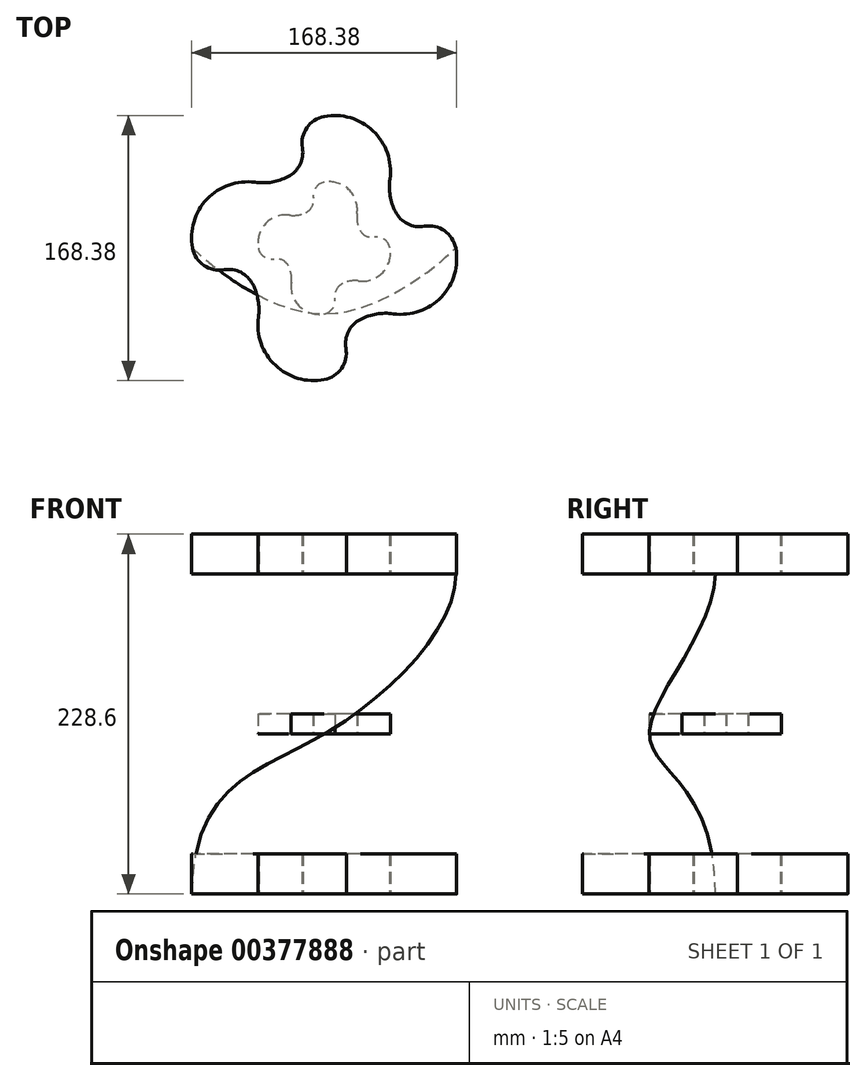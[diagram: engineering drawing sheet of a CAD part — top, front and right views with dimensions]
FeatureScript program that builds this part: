
annotation { "Feature Type Name" : "Feature", "Feature Type Description" : "" }
export const myFeature = defineFeature(function(context is Context, id is Id, definition is map)
    precondition{}
    {
        {
            var Q0;
            Q0=qCreatedBy(makeId("Top.planeOp"),FACE);
            var sketch = newSketch(context, id + "F0", { "sketchPlane" : qUnion([Q0])});
            skCircle(sketch, "E0", {"center": v(0, 0) * mm, "radius": 50.8 * mm, "construction": true});
            skArc(sketch, "E1", {"start": v(-23.02, 45.28) * mm, "mid": v(-15.4, 52.95) * mm, "end": v(-13.81, 63.64) * mm});
            skArc(sketch, "E2", {"start": v(0, 83.56) * mm, "mid": v(-10.98, 76.42) * mm, "end": v(-13.81, 63.64) * mm});
            skArc(sketch, "E3", {"start": v(41.76, 43.9) * mm, "mid": v(31.05, 74.44) * mm, "end": v(0, 83.56) * mm});
            skArc(sketch, "E4", {"start": v(41.76, 43.9) * mm, "mid": v(41.93, 33.2) * mm, "end": v(45.28, 23.02) * mm});
            skArc(sketch, "E5.1.0", {"start": v(-45.28, -23.02) * mm, "mid": v(-52.95, -15.4) * mm, "end": v(-63.64, -13.81) * mm});
            skArc(sketch, "E5.1.1", {"start": v(-83.56, 0) * mm, "mid": v(-76.42, -10.98) * mm, "end": v(-63.64, -13.81) * mm});
            skArc(sketch, "E5.1.2", {"start": v(-43.9, 41.76) * mm, "mid": v(-74.44, 31.05) * mm, "end": v(-83.56, 0) * mm});
            skArc(sketch, "E5.1.3", {"start": v(-43.9, 41.76) * mm, "mid": v(-33.2, 41.93) * mm, "end": v(-23.02, 45.28) * mm});
            skArc(sketch, "E5.2.0", {"start": v(23.02, -45.28) * mm, "mid": v(15.4, -52.95) * mm, "end": v(13.81, -63.64) * mm});
            skArc(sketch, "E5.2.1", {"start": v(0, -83.56) * mm, "mid": v(10.98, -76.42) * mm, "end": v(13.81, -63.64) * mm});
            skArc(sketch, "E5.2.2", {"start": v(-41.76, -43.9) * mm, "mid": v(-31.05, -74.44) * mm, "end": v(0, -83.56) * mm});
            skArc(sketch, "E5.2.3", {"start": v(-41.76, -43.9) * mm, "mid": v(-41.93, -33.2) * mm, "end": v(-45.28, -23.02) * mm});
            skArc(sketch, "E6.2.3.0", {"start": v(45.28, 23.02) * mm, "mid": v(52.95, 15.4) * mm, "end": v(63.64, 13.81) * mm});
            skArc(sketch, "E6.4.3.0", {"start": v(83.56, 0) * mm, "mid": v(76.42, 10.98) * mm, "end": v(63.64, 13.81) * mm});
            skArc(sketch, "E6.8.3.0", {"start": v(43.9, -41.76) * mm, "mid": v(74.44, -31.05) * mm, "end": v(83.56, 0) * mm});
            skArc(sketch, "E6.12.3.0", {"start": v(43.9, -41.76) * mm, "mid": v(33.2, -41.93) * mm, "end": v(23.02, -45.28) * mm});
            skSolve(sketch);
        }
        {
            var Q0;
            Q0=makeQuery(id+"F0.imprint","IMPRINT",FACE,{"disambiguationData":[TD([[makeQuery(id+"F0.imprint","IMPRINT",EDGE,{"derivedFrom":sQuery(id+"F0.wireOp",EDGE,"E1")}),-1.0]])]});
            extrude(context, id + "F1", {"entities" : qUnion([Q0]), "depth" : 25.4 * mm});
        }
        {
            var Q0;
            Q0=makeQuery(id+"F1.opExtrude","SWEPT_BODY",BODY,{"disambiguationData":[OSD([sQuery(id+"F0.wireOp",EDGE,"E1"),sQuery(id+"F0.wireOp",EDGE,"E2"),sQuery(id+"F0.wireOp",EDGE,"E3"),sQuery(id+"F0.wireOp",EDGE,"E4"),sQuery(id+"F0.wireOp",EDGE,"E5.1.0"),sQuery(id+"F0.wireOp",EDGE,"E5.1.1"),sQuery(id+"F0.wireOp",EDGE,"E5.1.2"),sQuery(id+"F0.wireOp",EDGE,"E5.1.3"),sQuery(id+"F0.wireOp",EDGE,"E5.2.0"),sQuery(id+"F0.wireOp",EDGE,"E5.2.1"),sQuery(id+"F0.wireOp",EDGE,"E5.2.2"),sQuery(id+"F0.wireOp",EDGE,"E5.2.3"),sQuery(id+"F0.wireOp",EDGE,"E6.2.3.0"),sQuery(id+"F0.wireOp",EDGE,"E6.4.3.0"),sQuery(id+"F0.wireOp",EDGE,"E6.8.3.0"),sQuery(id+"F0.wireOp",EDGE,"E6.12.3.0"),sQuery(id+"F0.wireOp",EDGE,"E6.2.4.0"),sQuery(id+"F0.wireOp",EDGE,"E6.4.4.0"),sQuery(id+"F0.wireOp",EDGE,"E6.8.4.0"),sQuery(id+"F0.wireOp",EDGE,"E6.12.4.0")])]});
            var Q1;
            Q1=qCreatedBy(makeId("Origin.pointOp"),VERTEX);
            transform(context, id + "F2", {"entities" : qUnion([Q0]), "transformType" : TransformType.TRANSLATION_3D, "dx" : 0 * mm, "dy" : 0 * mm, "dz" : 101.6 * mm, "makeCopy" : true});
        }
        {
            var Q0;
            Q0=makeQuery(id+"F2.opPattern","COPY",BODY,{"derivedFrom":makeQuery(id+"F1.opExtrude","SWEPT_BODY",BODY,{"disambiguationData":[OSD([sQuery(id+"F0.wireOp",EDGE,"E1"),sQuery(id+"F0.wireOp",EDGE,"E2"),sQuery(id+"F0.wireOp",EDGE,"E3"),sQuery(id+"F0.wireOp",EDGE,"E4"),sQuery(id+"F0.wireOp",EDGE,"E5.1.0"),sQuery(id+"F0.wireOp",EDGE,"E5.1.1"),sQuery(id+"F0.wireOp",EDGE,"E5.1.2"),sQuery(id+"F0.wireOp",EDGE,"E5.1.3"),sQuery(id+"F0.wireOp",EDGE,"E5.2.0"),sQuery(id+"F0.wireOp",EDGE,"E5.2.1"),sQuery(id+"F0.wireOp",EDGE,"E5.2.2"),sQuery(id+"F0.wireOp",EDGE,"E5.2.3"),sQuery(id+"F0.wireOp",EDGE,"E6.2.3.0"),sQuery(id+"F0.wireOp",EDGE,"E6.4.3.0"),sQuery(id+"F0.wireOp",EDGE,"E6.8.3.0"),sQuery(id+"F0.wireOp",EDGE,"E6.12.3.0"),sQuery(id+"F0.wireOp",EDGE,"E6.2.4.0"),sQuery(id+"F0.wireOp",EDGE,"E6.4.4.0"),sQuery(id+"F0.wireOp",EDGE,"E6.8.4.0"),sQuery(id+"F0.wireOp",EDGE,"E6.12.4.0")])]}),"instanceName":"1"});
            transform(context, id + "F3", {"entities" : qUnion([Q0]), "transformType" : TransformType.TRANSLATION_3D, "dx" : 0 * mm, "dy" : 0 * mm, "dz" : 101.6 * mm, "makeCopy" : true});
        }
        {
            var Q0;
            Q0=makeQuery(id+"F2.opPattern","COPY",FACE,{"derivedFrom":makeQuery(id+"F1.opExtrude","CAP_FACE",FACE,{"disambiguationData":[OSD([sQuery(id+"F0.wireOp",EDGE,"E1"),sQuery(id+"F0.wireOp",EDGE,"E2"),sQuery(id+"F0.wireOp",EDGE,"E3"),sQuery(id+"F0.wireOp",EDGE,"E4"),sQuery(id+"F0.wireOp",EDGE,"E5.1.0"),sQuery(id+"F0.wireOp",EDGE,"E5.1.1"),sQuery(id+"F0.wireOp",EDGE,"E5.1.2"),sQuery(id+"F0.wireOp",EDGE,"E5.1.3"),sQuery(id+"F0.wireOp",EDGE,"E5.2.0"),sQuery(id+"F0.wireOp",EDGE,"E5.2.1"),sQuery(id+"F0.wireOp",EDGE,"E5.2.2"),sQuery(id+"F0.wireOp",EDGE,"E5.2.3"),sQuery(id+"F0.wireOp",EDGE,"E6.2.3.0"),sQuery(id+"F0.wireOp",EDGE,"E6.4.3.0"),sQuery(id+"F0.wireOp",EDGE,"E6.8.3.0"),sQuery(id+"F0.wireOp",EDGE,"E6.12.3.0"),sQuery(id+"F0.wireOp",EDGE,"E6.2.4.0"),sQuery(id+"F0.wireOp",EDGE,"E6.4.4.0"),sQuery(id+"F0.wireOp",EDGE,"E6.8.4.0"),sQuery(id+"F0.wireOp",EDGE,"E6.12.4.0")])],"isStart":true}),"instanceName":"1"});
            var sketch = newSketch(context, id + "F4", { "sketchPlane" : qUnion([Q0])});
            skPoint(sketch, "E7", {"position": v(0, 0) * mm});
            skSolve(sketch);
        }
        {
            var Q0;
            Q0=makeQuery(id+"F2.opPattern","COPY",BODY,{"derivedFrom":makeQuery(id+"F1.opExtrude","SWEPT_BODY",BODY,{"disambiguationData":[OSD([sQuery(id+"F0.wireOp",EDGE,"E1"),sQuery(id+"F0.wireOp",EDGE,"E2"),sQuery(id+"F0.wireOp",EDGE,"E3"),sQuery(id+"F0.wireOp",EDGE,"E4"),sQuery(id+"F0.wireOp",EDGE,"E5.1.0"),sQuery(id+"F0.wireOp",EDGE,"E5.1.1"),sQuery(id+"F0.wireOp",EDGE,"E5.1.2"),sQuery(id+"F0.wireOp",EDGE,"E5.1.3"),sQuery(id+"F0.wireOp",EDGE,"E5.2.0"),sQuery(id+"F0.wireOp",EDGE,"E5.2.1"),sQuery(id+"F0.wireOp",EDGE,"E5.2.2"),sQuery(id+"F0.wireOp",EDGE,"E5.2.3"),sQuery(id+"F0.wireOp",EDGE,"E6.2.3.0"),sQuery(id+"F0.wireOp",EDGE,"E6.4.3.0"),sQuery(id+"F0.wireOp",EDGE,"E6.8.3.0"),sQuery(id+"F0.wireOp",EDGE,"E6.12.3.0"),sQuery(id+"F0.wireOp",EDGE,"E6.2.4.0"),sQuery(id+"F0.wireOp",EDGE,"E6.4.4.0"),sQuery(id+"F0.wireOp",EDGE,"E6.8.4.0"),sQuery(id+"F0.wireOp",EDGE,"E6.12.4.0")])]}),"instanceName":"1"});
            var Q1;
            Q1=sQuery(id+"F4.wireOp",VERTEX,"E7");
            transform(context, id + "F5", {"entities" : qUnion([Q0]), "transformType" : TransformType.SCALE_UNIFORMLY, "scale" : .5, "scalePoint" : qUnion([Q1]), "makeCopy" : false});
        }
        {
            var Q0;
            Q0=makeQuery(id+"F1.opExtrude","CAP_FACE",FACE,{"disambiguationData":[OSD([sQuery(id+"F0.wireOp",EDGE,"E1"),sQuery(id+"F0.wireOp",EDGE,"E2"),sQuery(id+"F0.wireOp",EDGE,"E3"),sQuery(id+"F0.wireOp",EDGE,"E4"),sQuery(id+"F0.wireOp",EDGE,"E5.1.0"),sQuery(id+"F0.wireOp",EDGE,"E5.1.1"),sQuery(id+"F0.wireOp",EDGE,"E5.1.2"),sQuery(id+"F0.wireOp",EDGE,"E5.1.3"),sQuery(id+"F0.wireOp",EDGE,"E5.2.0"),sQuery(id+"F0.wireOp",EDGE,"E5.2.1"),sQuery(id+"F0.wireOp",EDGE,"E5.2.2"),sQuery(id+"F0.wireOp",EDGE,"E5.2.3"),sQuery(id+"F0.wireOp",EDGE,"E6.2.3.0"),sQuery(id+"F0.wireOp",EDGE,"E6.4.3.0"),sQuery(id+"F0.wireOp",EDGE,"E6.8.3.0"),sQuery(id+"F0.wireOp",EDGE,"E6.12.3.0"),sQuery(id+"F0.wireOp",EDGE,"E6.2.4.0"),sQuery(id+"F0.wireOp",EDGE,"E6.4.4.0"),sQuery(id+"F0.wireOp",EDGE,"E6.8.4.0"),sQuery(id+"F0.wireOp",EDGE,"E6.12.4.0")])],"isStart":true});
            var Q1;
            Q1=makeQuery(id+"F2.opPattern","COPY",FACE,{"derivedFrom":makeQuery(id+"F1.opExtrude","CAP_FACE",FACE,{"disambiguationData":[OSD([sQuery(id+"F0.wireOp",EDGE,"E1"),sQuery(id+"F0.wireOp",EDGE,"E2"),sQuery(id+"F0.wireOp",EDGE,"E3"),sQuery(id+"F0.wireOp",EDGE,"E4"),sQuery(id+"F0.wireOp",EDGE,"E5.1.0"),sQuery(id+"F0.wireOp",EDGE,"E5.1.1"),sQuery(id+"F0.wireOp",EDGE,"E5.1.2"),sQuery(id+"F0.wireOp",EDGE,"E5.1.3"),sQuery(id+"F0.wireOp",EDGE,"E5.2.0"),sQuery(id+"F0.wireOp",EDGE,"E5.2.1"),sQuery(id+"F0.wireOp",EDGE,"E5.2.2"),sQuery(id+"F0.wireOp",EDGE,"E5.2.3"),sQuery(id+"F0.wireOp",EDGE,"E6.2.3.0"),sQuery(id+"F0.wireOp",EDGE,"E6.4.3.0"),sQuery(id+"F0.wireOp",EDGE,"E6.8.3.0"),sQuery(id+"F0.wireOp",EDGE,"E6.12.3.0"),sQuery(id+"F0.wireOp",EDGE,"E6.2.4.0"),sQuery(id+"F0.wireOp",EDGE,"E6.4.4.0"),sQuery(id+"F0.wireOp",EDGE,"E6.8.4.0"),sQuery(id+"F0.wireOp",EDGE,"E6.12.4.0")])],"isStart":true}),"instanceName":"1"});
            var Q2;
            Q2=makeQuery(id+"F3.opPattern","COPY",FACE,{"derivedFrom":makeQuery(id+"F2.opPattern","COPY",FACE,{"derivedFrom":makeQuery(id+"F1.opExtrude","CAP_FACE",FACE,{"disambiguationData":[OSD([sQuery(id+"F0.wireOp",EDGE,"E1"),sQuery(id+"F0.wireOp",EDGE,"E2"),sQuery(id+"F0.wireOp",EDGE,"E3"),sQuery(id+"F0.wireOp",EDGE,"E4"),sQuery(id+"F0.wireOp",EDGE,"E5.1.0"),sQuery(id+"F0.wireOp",EDGE,"E5.1.1"),sQuery(id+"F0.wireOp",EDGE,"E5.1.2"),sQuery(id+"F0.wireOp",EDGE,"E5.1.3"),sQuery(id+"F0.wireOp",EDGE,"E5.2.0"),sQuery(id+"F0.wireOp",EDGE,"E5.2.1"),sQuery(id+"F0.wireOp",EDGE,"E5.2.2"),sQuery(id+"F0.wireOp",EDGE,"E5.2.3"),sQuery(id+"F0.wireOp",EDGE,"E6.2.3.0"),sQuery(id+"F0.wireOp",EDGE,"E6.4.3.0"),sQuery(id+"F0.wireOp",EDGE,"E6.8.3.0"),sQuery(id+"F0.wireOp",EDGE,"E6.12.3.0"),sQuery(id+"F0.wireOp",EDGE,"E6.2.4.0"),sQuery(id+"F0.wireOp",EDGE,"E6.4.4.0"),sQuery(id+"F0.wireOp",EDGE,"E6.8.4.0"),sQuery(id+"F0.wireOp",EDGE,"E6.12.4.0")])],"isStart":true}),"instanceName":"1"}),"instanceName":"1"});
            var Q3;
            Q3=makeQuery(id+"F1.opExtrude","CAP_VERTEX",VERTEX,{"disambiguationData":[OSD([sQuery(id+"F0.wireOp",EDGE,"E5.1.1"),sQuery(id+"F0.wireOp",EDGE,"E5.1.2")])],"isStart":true});
            var Q4;
            Q4=makeQuery(id+"F2.opPattern","COPY",VERTEX,{"derivedFrom":makeQuery(id+"F1.opExtrude","CAP_VERTEX",VERTEX,{"disambiguationData":[OSD([sQuery(id+"F0.wireOp",EDGE,"E5.2.1"),sQuery(id+"F0.wireOp",EDGE,"E5.2.2")])],"isStart":true}),"instanceName":"1"});
            var Q5;
            Q5=makeQuery(id+"F3.opPattern","COPY",VERTEX,{"derivedFrom":makeQuery(id+"F2.opPattern","COPY",VERTEX,{"derivedFrom":makeQuery(id+"F1.opExtrude","CAP_VERTEX",VERTEX,{"disambiguationData":[OSD([sQuery(id+"F0.wireOp",EDGE,"E6.4.3.0"),sQuery(id+"F0.wireOp",EDGE,"E6.8.3.0")])],"isStart":true}),"instanceName":"1"}),"instanceName":"1"});
            loft(context, id + "F6", {"startCondition" : LoftEndDerivativeType.NORMAL_TO_PROFILE, "startMagnitude" : 2, "endCondition" : LoftEndDerivativeType.NORMAL_TO_PROFILE, "endMagnitude" : 1, "sheetProfilesArray" : [{ "sheetProfileEntities" : qUnion([Q0]) }, { "sheetProfileEntities" : qUnion([Q1]) }, { "sheetProfileEntities" : qUnion([Q2]) }], "matchConnections" : true, "connections" : [{ "connectionEntities" : qUnion([Q3, Q4, Q5]), "connectionEdgeQueries" : qUnion([]), "connectionEdgeParameters" : [] }]});
        }
    });
